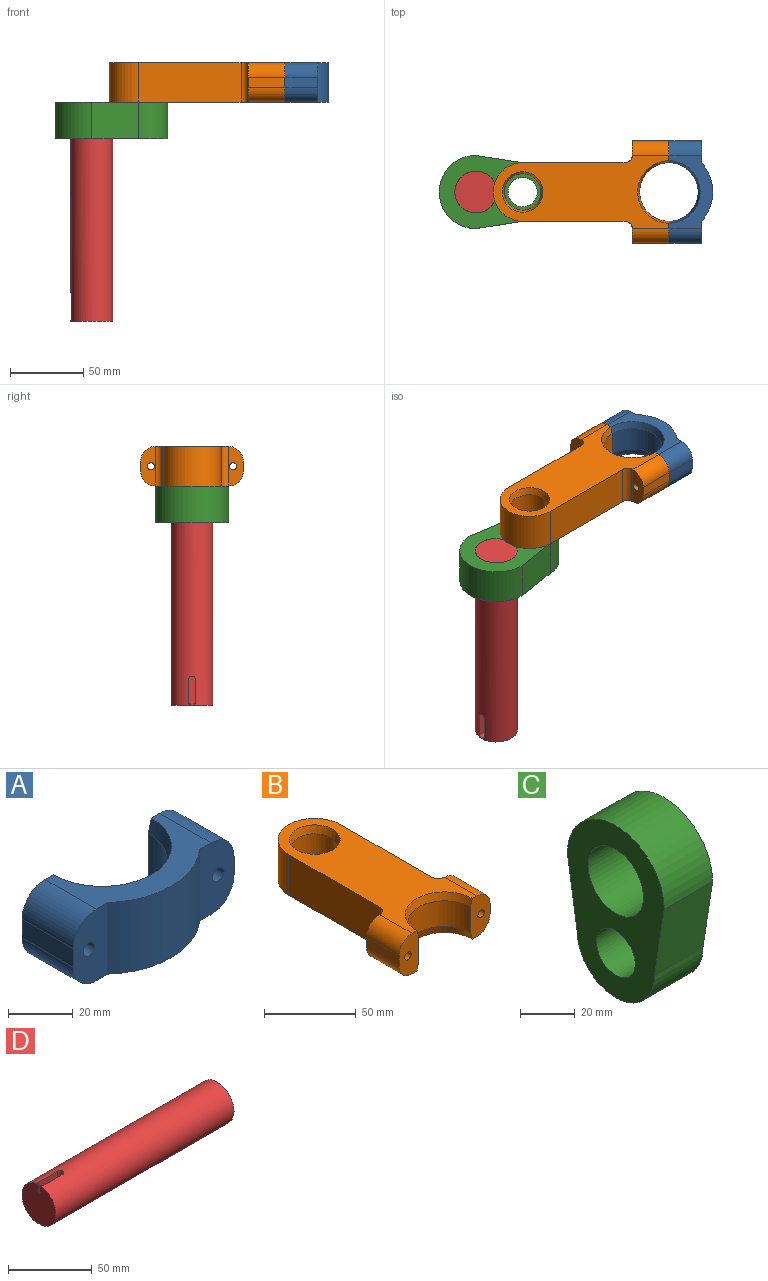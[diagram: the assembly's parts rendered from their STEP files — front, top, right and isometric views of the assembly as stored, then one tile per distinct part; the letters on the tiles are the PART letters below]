
ASSEMBLY  parts=4 mates=5
PART A: 18 faces, bbox 70x30x27 mm
  f0: plane 22.36x7mm, normal (-1,0,0), area 156.5mm2, adj f1,f7,f15,f17
  f1: plane 27x15mm, normal (0,-1,0), area 342.4mm2, adj f0,f2,f8,f9,f12,f15,f17
  f2: cylinder r=30mm len=40mm, axis (0,0,-1), area 1182.2mm2, adj f1,f3,f8,f9
  f3: plane 27x15mm, normal (0,-1,0), area 342.4mm2, adj f2,f4,f8,f9,f13,f14,f16
  f4: plane 22.36x7mm, normal (1,0,0), area 156.5mm2, adj f3,f5,f14,f16
  f5: plane 27x15mm, normal (0,1,0), area 335.7mm2, adj f4,f6,f8,f9,f10,f11,f13,f14
  f6: cylinder r=20mm len=40mm, axis (0,0,-1), area 1068.1mm2, adj f5,f7,f10,f11
  f7: plane 27x15mm, normal (0,1,0), area 335.7mm2, adj f0,f6,f8,f9,f10,f11,f12,f15
  f8: plane 50x30mm, normal (0,0,1), area 612.3mm2, adj f1,f2,f3,f5,f7,f11,f16,f17
  f9: plane 50x30mm, normal (0,0,-1), area 612.3mm2, adj f1,f2,f3,f5,f7,f10,f14,f15
  f10: cone r=20mm half-angle=15deg, axis (0,0,-1), area 336.1mm2, adj f5,f6,f7,f9
  f11: cone r=21.34mm half-angle=15deg, axis (0,0,1), area 336.1mm2, adj f5,f6,f7,f8
  f12: cylinder r=2.5mm len=22.36mm, axis (0,1,0), area 351.2mm2, adj f1,f7
  f13: cylinder r=2.5mm len=22.36mm, axis (0,1,0), area 351.2mm2, adj f3,f5
  f14: cylinder r=10mm len=22.36mm, axis (0,1,0), area 351.2mm2, adj f3,f4,f5,f9
  f15: cylinder r=10mm len=22.36mm, axis (0,-1,0), area 351.2mm2, adj f0,f1,f7,f9
  f16: cylinder r=10mm len=22.36mm, axis (0,-1,0), area 351.2mm2, adj f3,f4,f5,f8
  f17: cylinder r=10mm len=22.36mm, axis (0,1,0), area 351.2mm2, adj f0,f1,f7,f8
PART B: 25 faces, bbox 70x120x27 mm
  f0: cylinder r=20mm len=40mm, axis (0,0,-1), area 1068.1mm2, adj f1,f9,f15,f17
  f1: plane 27x15mm, normal (0,-1,0), area 335.7mm2, adj f0,f2,f11,f12,f15,f17,f19,f21
  f2: plane 25x7mm, normal (1,0,0), area 175mm2, adj f1,f3,f21,f23
  f3: plane 27x10mm, normal (0,1,0), area 207.4mm2, adj f2,f13,f19,f21,f23
  f4: plane 70x27mm, normal (1,0,0), area 1890mm2, adj f5,f11,f12,f13
  f5: cylinder r=20mm len=40mm, axis (0,0,-1), area 1696.5mm2, adj f4,f6,f11,f12
  f6: plane 70x27mm, normal (-1,0,0), area 1890mm2, adj f5,f11,f12,f14
  f7: plane 27x10mm, normal (0,1,0), area 207.4mm2, adj f8,f14,f18,f20,f22
  f8: plane 25x7mm, normal (-1,0,0), area 175mm2, adj f7,f9,f20,f22
  f9: plane 27x15mm, normal (0,-1,0), area 335.7mm2, adj f0,f8,f11,f12,f15,f17,f18,f20
  f10: cylinder r=12.5mm len=25mm, axis (0,0,-1), area 1335.2mm2, adj f16,f24
  f11: plane 120x50mm, normal (0,0,1), area 3572mm2, adj f1,f4,f5,f6,f9,f13,f14,f16
  f12: plane 120x50mm, normal (0,0,-1), area 3572mm2, adj f1,f4,f5,f6,f9,f13,f14,f15
  f13: cylinder r=5mm len=27mm, axis (0,0,-1), area 212.1mm2, adj f3,f4,f11,f12
  f14: cylinder r=5mm len=27mm, axis (0,0,-1), area 212.1mm2, adj f6,f7,f11,f12
  f15: cone r=21.34mm half-angle=15deg, axis (0,0,-1), area 336.1mm2, adj f0,f1,f9,f12
  f16: cone r=12.5mm half-angle=15deg, axis (0,0,1), area 428.3mm2, adj f10,f11
  f17: cone r=20mm half-angle=15deg, axis (0,0,1), area 336.1mm2, adj f0,f1,f9,f11
  f18: cylinder r=2.5mm len=25mm, axis (0,-1,0), area 392.7mm2, adj f7,f9
  f19: cylinder r=2.5mm len=25mm, axis (0,-1,0), area 392.7mm2, adj f1,f3
  f20: cylinder r=10mm len=25mm, axis (0,-1,0), area 392.7mm2, adj f7,f8,f9,f12
  f21: cylinder r=10mm len=25mm, axis (0,1,0), area 392.7mm2, adj f1,f2,f3,f12
  f22: cylinder r=10mm len=25mm, axis (0,1,0), area 392.7mm2, adj f7,f8,f9,f11
  f23: cylinder r=10mm len=25mm, axis (0,-1,0), area 392.7mm2, adj f1,f2,f3,f11
  f24: cone r=13.84mm half-angle=15deg, axis (0,0,-1), area 428.3mm2, adj f10,f12
PART C: 8 faces, bbox 25x50x77 mm
  f0: cylinder r=25mm len=50mm, axis (-1,0,0), area 1963.5mm2, adj f1,f5,f6,f7
  f1: plane 32x25mm, normal (0,-0.99,-0.15), area 809.7mm2, adj f0,f2,f6,f7
  f2: cylinder r=20mm len=40mm, axis (-1,0,0), area 1570.8mm2, adj f1,f5,f6,f7
  f3: cylinder r=14.3mm len=28.6mm, axis (-1,0,0), area 2246.2mm2, adj f6,f7
  f4: cylinder r=10mm len=25mm, axis (-1,0,0), area 1570.8mm2, adj f6,f7
  f5: plane 32x25mm, normal (0,0.99,-0.15), area 809.7mm2, adj f0,f2,f6,f7
  f6: plane 77x50mm, normal (1,0,0), area 2093.5mm2, adj f0,f1,f2,f3,f4,f5
  f7: plane 77x50mm, normal (-1,0,0), area 2093.5mm2, adj f0,f1,f2,f3,f4,f5
PART D: 11 faces, bbox 150x28.6x28.6 mm
  f0: cylinder r=14.3mm len=150mm, axis (-1,0,0), area 13390.5mm2, adj f1,f2,f3,f4,f5,f6,f7,f8
  f1: plane 28.6x28.6mm, normal (1,0,0), area 642.4mm2, adj f0
  f2: plane 28.6x28.6mm, normal (-1,0,0), area 639.9mm2, adj f0,f8,f9,f10
  f3: plane 5x0.5mm, normal (-1,0,0), area 2.5mm2, adj f0,f4,f7,f10
  f4: cylinder r=2mm len=5mm, axis (0,0,1), area 15.4mm2, adj f0,f3,f5,f10
  f5: plane 16x4.82mm, normal (0,-1,0), area 77.2mm2, adj f0,f4,f8,f10
  f6: plane 16x4.82mm, normal (0,1,0), area 77.2mm2, adj f0,f7,f9,f10
  f7: cylinder r=2mm len=5mm, axis (0,0,1), area 15.4mm2, adj f0,f3,f6,f10
  f8: cylinder r=2mm len=5mm, axis (0,0,1), area 15.4mm2, adj f0,f2,f5,f10
  f9: cylinder r=2mm len=5mm, axis (0,0,1), area 15.4mm2, adj f0,f2,f6,f10
  f10: plane 20x4.5mm, normal (0,0,1), area 86.6mm2, adj f2,f3,f4,f5,f6,f7,f8,f9
PLACE A rot(axis=(0,0,1),90deg) t=(232.43,226.94,62.84)mm
PLACE B rot(axis=(0,0,1),90deg) t=(232.44,226.94,62.84)mm
PLACE C rot(axis=(0,-1,0),90deg) t=(100.44,226.94,24.34)mm
PLACE D rot(axis=(0,-1,0),90deg) t=(100.44,226.94,-100.66)mm
MATE parallel D.f0 <-> C.f6  axis (0,0,1) through (100.44,226.94,49.34)mm
MATE parallel B.f12 <-> C.f6  axis (0,0,-1) through (175.07,226.94,49.34)mm
MATE revolute A.f12 <-> B.f18  axis (-1,0,0) through (232.44,198.77,62.84)mm
MATE parallel C.f2 <-> B.f5  axis (0,0,-1) through (132.44,226.94,24.34)mm
MATE slider D.f0 <-> C.f3  axis (0,0,-1) through (100.44,226.94,-25.66)mm
